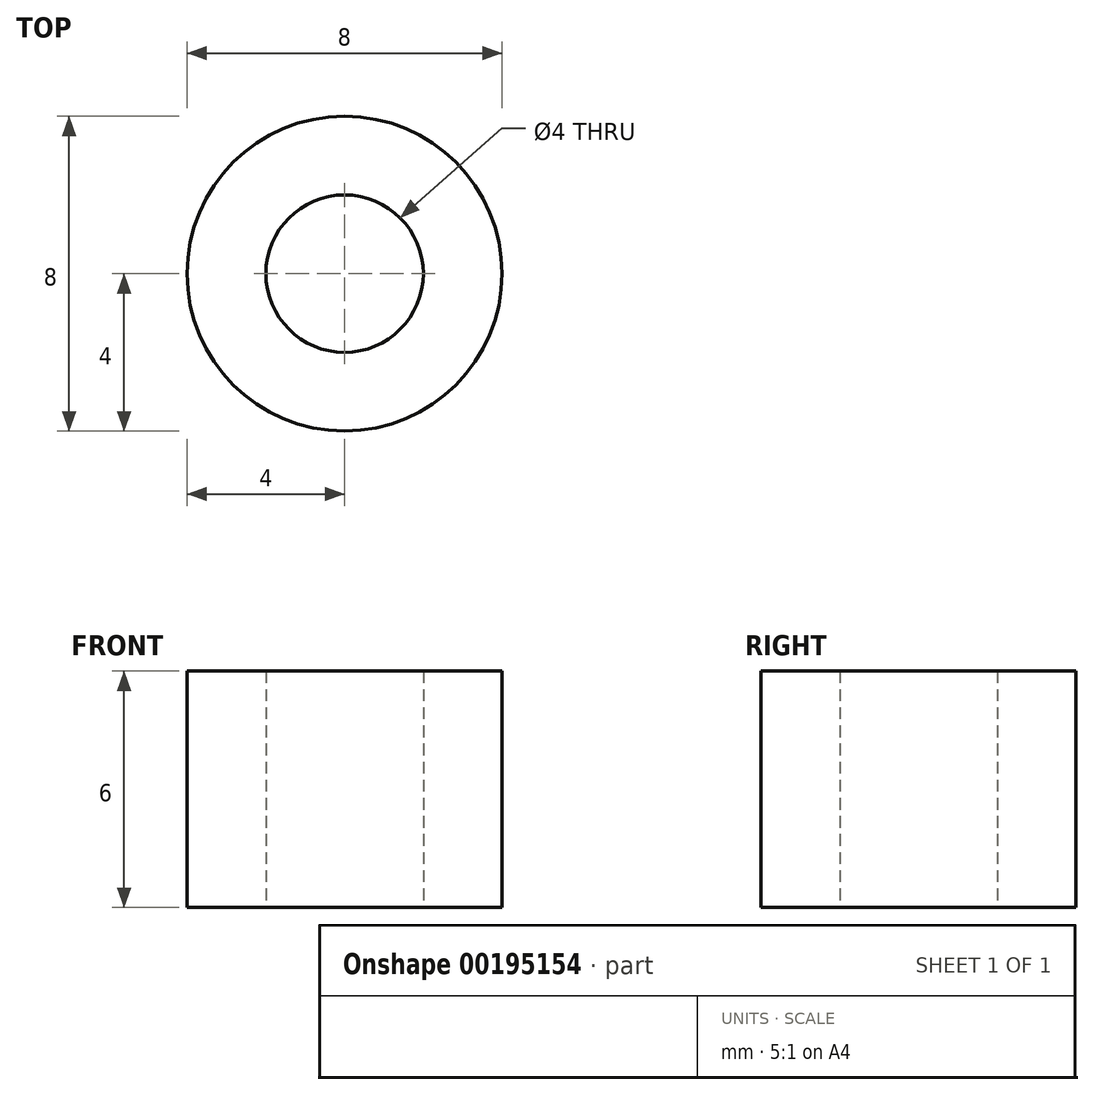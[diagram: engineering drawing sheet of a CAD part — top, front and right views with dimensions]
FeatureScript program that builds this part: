
annotation { "Feature Type Name" : "Feature", "Feature Type Description" : "" }
export const myFeature = defineFeature(function(context is Context, id is Id, definition is map)
    precondition{}
    {
        {
            var Q0;
            Q0=qCreatedBy(makeId("Top.planeOp"),FACE);
            var sketch = newSketch(context, id + "F0", { "sketchPlane" : qUnion([Q0])});
            skCircle(sketch, "E0", {"center": v(0, 0) * mm, "radius": 2 * mm});
            skCircle(sketch, "E1.0", {"center": v(0, 0) * mm, "radius": 4 * mm});
            skSolve(sketch);
        }
        {
            var Q0;
            Q0 = qSketchRegion(id + "F0", true);
            extrude(context, id + "F1", {"entities" : qUnion([Q0]), "depth" : 6 * mm});
        }
    });
